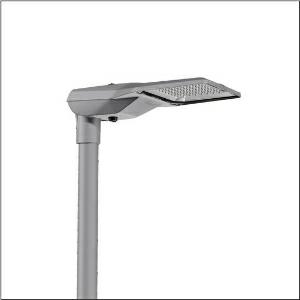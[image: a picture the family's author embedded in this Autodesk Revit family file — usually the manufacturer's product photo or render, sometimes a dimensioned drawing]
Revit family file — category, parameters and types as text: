
# Revit family: streetlight_sl_21_midi___stw1_0a_5xe3e43t08nb_27ab
name_source: partatom
category: Lighting Fixtures
units: mm (PartAtom-declared; Revit-internal decimal feet)

## family parameters
Cut with Voids When Loaded = No
Host = Face
Light Source = No
Part Type = Normal
Room Calculation Point = No
Round Connector Dimension = Use Diameter
Shared = No

## types (1)
- --- (1 x LED, 23710 lm, 151.2 W, 4000K)
    Apparent Load = 151 VA
    CIE Flux Codes = 39 75 98 100 100
    Color Rendering = 70
    Color Temperature = 4000K
    Default Elevation = 1800 mm
    Description = Streetlight SL 21 midi, mast luminaire, primary light control with lens, of PMMA, primary optical cover: cover, of toughened safety glass, transparent, light distribution: STW1.0a, light emission: direct distribution, primary light characteristic: asymmetric, installation type: side-entry, post-top, LED, High Power LED, rated luminous flux: 23.710lm, luminous efficacy: 157lm/W, light colour: 740, colour temperature: 4000K, control gear: D4i, control: overheat protection, constant luminous flux control, time-dependent luminous flux control, flexible luminous flux parameterisation, pre-setting: logarithmic dimming characteristic, mains connection: 230..240V, AC, 50/60Hz, start of lifetime: 151W, end of service life: 157W, reduction: 70W, luminaire housing, of diecast aluminium, powder-coated, SITECO metallic grey (DB 702S), corrosivity category C5 high according to DIN EN ISO 12944, please order mast flange separately, inclination adjustable: 0°, 5°, 10°, 15°, sealing non-destructively replaceable, multi-level sealing system, length: 644mm, width: 335mm, height: 110mm, mast flange for spigot size: 42mm (side-entry): 5XC10008XM4, 60/48mm (side-entry/post-top): 5XC10108XM2, 76/60mm (side-entry/post-top): 5XC10108XM1, mounting height: 4..8m, Smart Interface below and above, protection rating (complete): IP66, insulation class (complete): insulation class II (safety insulation), certification: CE, ENEC, ENEC+, VDE, impact resistance: IK10, permissible operating ambient temperature for outdoor applications: -40..+50°C, standard-compliant lighting for roads and squares, packaging unit: 1 piece

Light Distribution: STW1.0a
    Height = 111 mm
    Lamp = 1 x LED
    Lamp Light Flux = 23710 lm
    Lamp Power = 151.2 W
    Lamp count = 1
    Length = 644 mm
    Luminous efficacy = 157 lm/W
    Manufacturer = Siteco
    ModVariant = No
    Model = 5XE3E43T08NB
    Number of Poles = 1
    OnlyDefault = Yes
    Power Factor = 1
    Product Name = Streetlight SL 21 midi | STW1.0a
    Product group = mast luminaire | pylon top
    ProductGroupID = 6100
    Protection Class = Protection class II
    Protection Degree = IP 66
    RLX_Detail_Level = 1
    RLX_Emergency_Light_Flux = 0 lm
    RLX_Emergency_Type = 0
    RLX_Emergency_Type_DB = No
    RlxData = <blob elided: 27069 chars, md5=b067135b>
    Socket = socket
    Standby Power = 0 W
    System Light Flux = 23710 lm
    System Power = 151 W
    Type Comments = factory setting: luminous flux: 100 % | dim-lin: 254 | 802 mA
    Type Image = l_1004304.jpg
    URL = http://relux.com
    VarID = @adj_169011
    Voltage = 0 V
    Weight = 0.00 kg
    Width = 336 mm

## geometry (parser evidence)
native form markers: Blend x4, Sweep x10
no freeform markers — native parametric forms only
